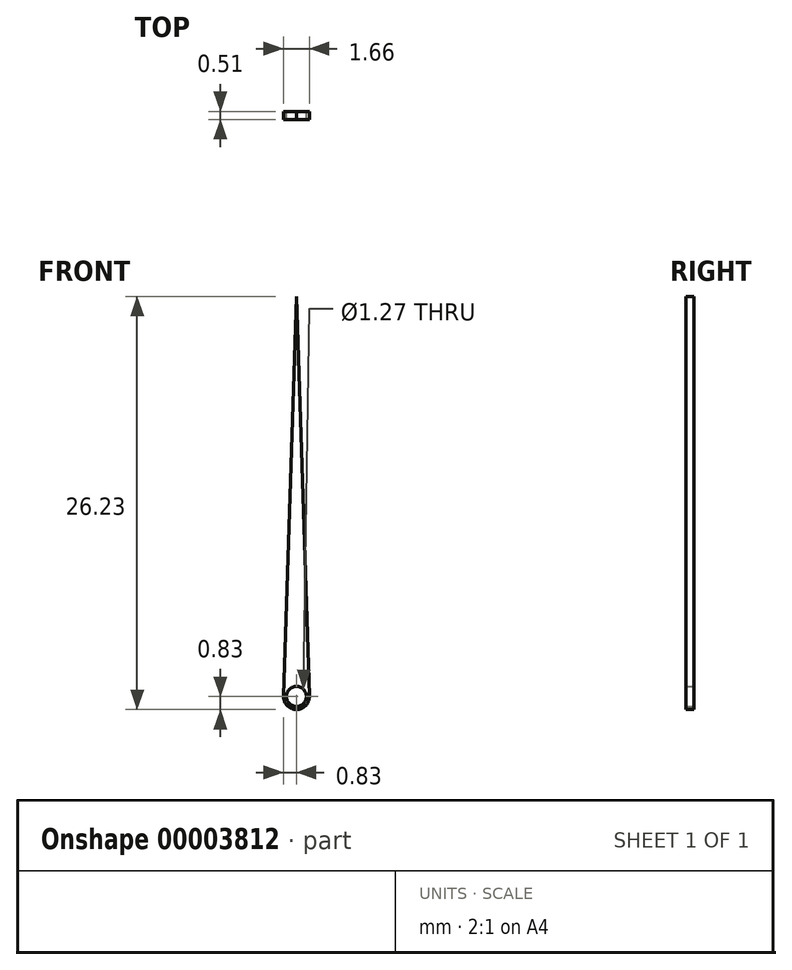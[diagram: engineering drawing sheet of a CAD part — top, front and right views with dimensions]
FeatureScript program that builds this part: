
annotation { "Feature Type Name" : "Feature", "Feature Type Description" : "" }
export const myFeature = defineFeature(function(context is Context, id is Id, definition is map)
    precondition{}
    {
        {
            var Q0;
            Q0=qCreatedBy(makeId("Front.planeOp"),FACE);
            var sketch = newSketch(context, id + "F0", { "sketchPlane" : qUnion([Q0])});
            skCircle(sketch, "E0", {"center": v(0, 0) * mm, "radius": 0.83 * mm});
            skPoint(sketch, "E1.start.orphan", {"position": v(0, 25.4) * mm});
            skPoint(sketch, "E2.orphan", {"position": v(-0.95, 0) * mm});
            skLineSegment(sketch, "E3", {"start": v(0, 0) * mm, "end": v(0, 25.4) * mm, "construction": true});
            skLineSegment(sketch, "E4", {"start": v(0, 25.4) * mm, "end": v(0, 25.4) * mm});
            skLineSegment(sketch, "E5", {"start": v(0, 25.4) * mm, "end": v(0.83, 0) * mm});
            skLineSegment(sketch, "E6.0.MirrorCS", {"start": v(0, 25.4) * mm, "end": v(-0.83, 0) * mm});
            skSolve(sketch);
        }
        {
            var Q0;
            {var subQ0=sQuery(id+"F0.wireOp",EDGE,"E0");var subQ3=sQuery(id+"F0.wireOp",EDGE,"E5");var subQ4=makeQuery(id+"F0.imprint","INTERSECT",VERTEX,{"derivedFrom":[subQ0,subQ3]});var subQ5=makeQuery(id+"F0.imprint","IMPRINT",EDGE,{"disambiguationData":[TD([[subQ4,-1.0]])],"derivedFrom":subQ0});Q0=qUnion([makeQuery(id+"F0.imprint","IMPRINT",FACE,{"disambiguationData":[TD([[subQ5,1.0]])]}),makeQuery(id+"F0.imprint","IMPRINT",FACE,{"disambiguationData":[TD([[subQ5,-1.0]])]})]);}
            extrude(context, id + "F1", {"entities" : qUnion([Q0]), "depth" : 0.5 * mm});
        }
        {
            var Q0;
            {var subQ0=sQuery(id+"F0.wireOp",EDGE,"E0");var subQ2=makeQuery(id+"F0.imprint","INTERSECT",VERTEX,{"derivedFrom":[subQ0,sQuery(id+"F0.wireOp",EDGE,"E5")]});Q0=makeQuery(id+"F0.imprint","IMPRINT",FACE,{"disambiguationData":[TD([[makeQuery(id+"F0.imprint","IMPRINT",EDGE,{"disambiguationData":[TD([[subQ2,-1.0]])],"derivedFrom":subQ0}),1.0]])]});}
            var sketch = newSketch(context, id + "F2", { "sketchPlane" : qUnion([Q0])});
            skCircle(sketch, "E7", {"center": v(0, 0) * mm, "radius": 0.64 * mm});
            skSolve(sketch);
        }
        {
            var Q0;
            Q0=makeQuery(id+"F2.imprint","IMPRINT",FACE,{"disambiguationData":[TD([[makeQuery(id+"F2.imprint","IMPRINT",EDGE,{"derivedFrom":sQuery(id+"F2.wireOp",EDGE,"E7")}),1.0]])]});
            extrude(context, id + "F3", {"entities" : qUnion([Q0]), "operationType" : NewBodyOperationType.REMOVE, "depth" : 25.4 * mm});
        }
    });
